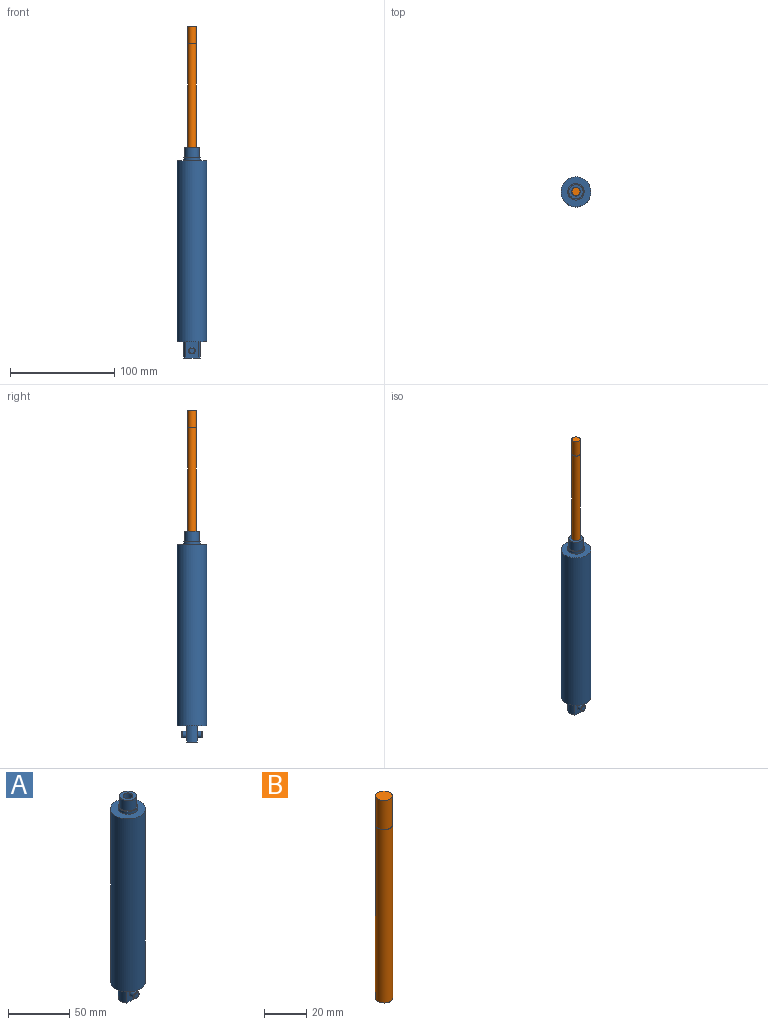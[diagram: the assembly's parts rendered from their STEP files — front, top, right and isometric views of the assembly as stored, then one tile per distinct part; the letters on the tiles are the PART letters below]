
ASSEMBLY  parts=2 mates=1
PART A: 20 faces, bbox 28.6x28.6x202 mm
  f0: cylinder r=7.9mm len=15.8mm, axis (0,0,1), area 165.3mm2, adj f1,f3,f12,f13
  f1: plane 15.8x9.72mm, normal (0,0,-1), area 143.2mm2, adj f0,f11,f12,f13
  f2: cylinder r=14.29mm len=173.23mm, axis (0,0,-1), area 15550.9mm2, adj f3,f4
  f3: plane 28.58x28.58mm, normal (0,0,-1), area 498.1mm2, adj f0,f2,f11,f12,f13
  f4: plane 28.58x28.58mm, normal (0,0,1), area 445.9mm2, adj f2,f5
  f5: cylinder r=7.89mm len=15.77mm, axis (0,0,-1), area 134.7mm2, adj f4,f6
  f6: plane 15.77x15.77mm, normal (0,0,1), area 47.7mm2, adj f5,f7
  f7: cylinder r=6.86mm len=13.72mm, axis (0,0,-1), area 439.4mm2, adj f6,f8
  f8: plane 13.72x13.72mm, normal (0,0,1), area 96.5mm2, adj f7,f9
  f9: cylinder r=4.04mm len=117.48mm, axis (0,0,1), area 2981mm2, adj f8,f10
  f10: plane 8.08x8.08mm, normal (0,0,1), area 51.2mm2, adj f9
  f11: cylinder r=7.9mm len=15.8mm, axis (0,0,1), area 165.3mm2, adj f1,f3,f12,f13
  f12: plane 15.8x12.46mm, normal (0,1,0), area 165.2mm2, adj f0,f1,f3,f11,f14
  f13: plane 15.8x12.46mm, normal (0,-1,0), area 165.2mm2, adj f0,f1,f3,f11,f16
  f14: cylinder r=3.17mm len=6.35mm, axis (0,-1,0), area 90.4mm2, adj f12,f19
  f15: plane 5.09x5.09mm, normal (0,1,0), area 20.2mm2, adj f19
  f16: cylinder r=3.17mm len=6.35mm, axis (0,1,0), area 90.4mm2, adj f13,f18
  f17: plane 5.09x5.09mm, normal (0,-1,0), area 20.2mm2, adj f18
  f18: bspline ~7.04x7.04mm, area 17.3mm2, adj f16,f17
  f19: bspline ~7.04x7.04mm, area 17.3mm2, adj f14,f15
PART B: 5 faces, bbox 8.1x8.1x117.5 mm
  f0: cylinder r=4.04mm len=100.57mm, axis (0,0,-1), area 2552mm2, adj f1,f3
  f1: plane 8.08x8.08mm, normal (0,0,-1), area 51.2mm2, adj f0
  f2: cylinder r=3.94mm len=16.9mm, axis (0,0,1), area 418.1mm2, adj f3,f4
  f3: plane 8.08x8.08mm, normal (0,0,1), area 2.5mm2, adj f0,f2
  f4: plane 7.87x7.87mm, normal (0,0,1), area 48.7mm2, adj f2
PLACE A rot(axis=(0,0,-1),0deg) t=(-122.38,53.61,43.7)mm
PLACE B t=(-122.38,53.61,42.48)mm
MATE slider A.f7 <-> B.f0  axis (0,0,1) through (-122.38,53.61,229.84)mm
